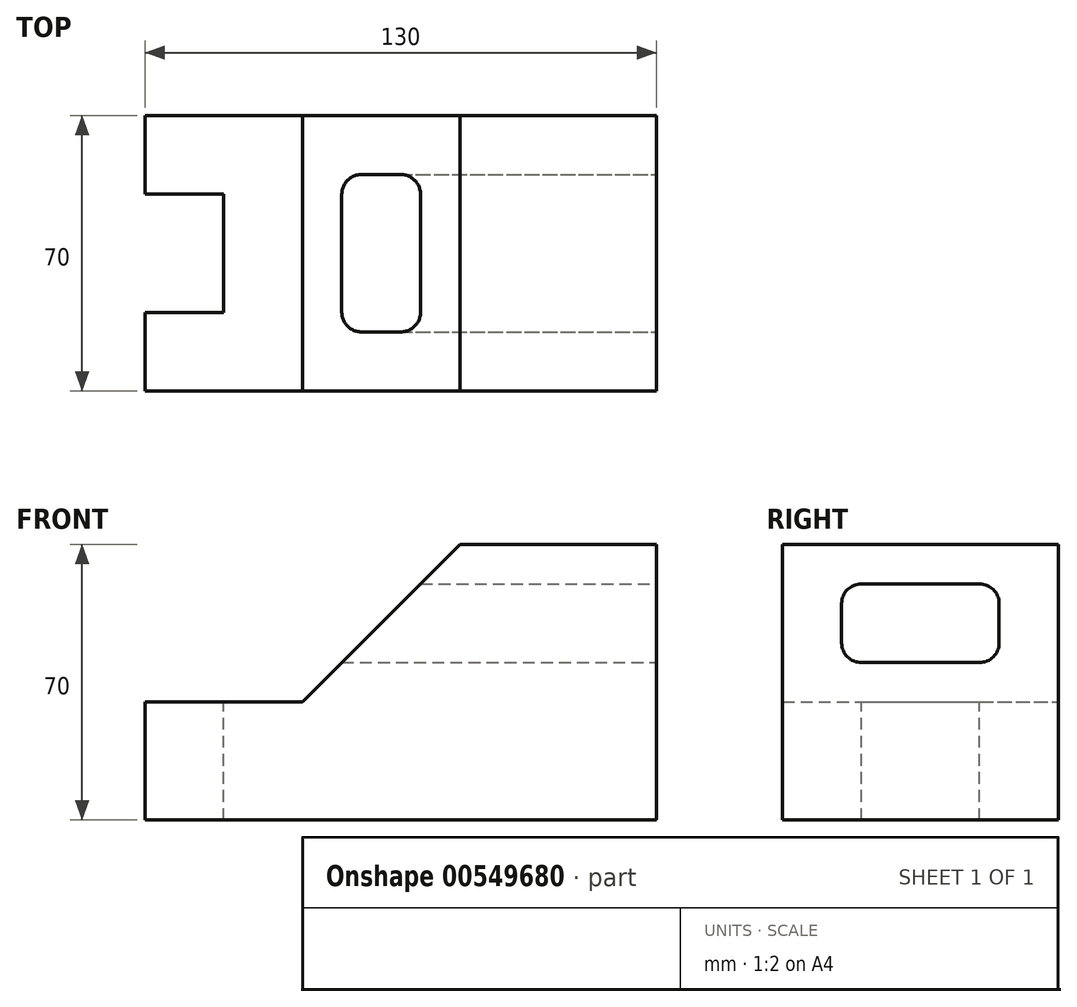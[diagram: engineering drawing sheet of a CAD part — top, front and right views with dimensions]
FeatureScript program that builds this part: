
annotation { "Feature Type Name" : "Feature", "Feature Type Description" : "" }
export const myFeature = defineFeature(function(context is Context, id is Id, definition is map)
    precondition{}
    {
        {
            var Q0;
            Q0=qCreatedBy(makeId("Front.planeOp"),FACE);
            var sketch = newSketch(context, id + "F0", { "sketchPlane" : qUnion([Q0])});
            skLineSegment(sketch, "E0.bottom", {"start": v(15, 35) * mm, "end": v(65, 35) * mm});
            skLineSegment(sketch, "E0.top", {"start": v(-65, -35) * mm, "end": v(65, -35) * mm});
            skLineSegment(sketch, "E0.left", {"start": v(-65, -5) * mm, "end": v(-65, -35) * mm});
            skLineSegment(sketch, "E0.right", {"start": v(65, 35) * mm, "end": v(65, -35) * mm});
            skPoint(sketch, "E0.middle", {"position": v(0, 0) * mm});
            skLineSegment(sketch, "E1", {"start": v(-65, -5) * mm, "end": v(-25, -5) * mm});
            skLineSegment(sketch, "E2", {"start": v(-25, -5) * mm, "end": v(15, 35) * mm});
            skPoint(sketch, "E3.orphan", {"position": v(-65, 35) * mm});
            skSolve(sketch);
        }
        {
            var Q0;
            Q0 = qSketchRegion(id + "F0", true);
            extrude(context, id + "F1", {"entities" : qUnion([Q0]), "depth" : 70 * mm, "offsetDistance" : 25 * mm});
        }
        {
            var Q0;
            Q0=makeQuery(id+"F1.opExtrude","SWEPT_FACE",FACE,{"disambiguationData":[OSD([sQuery(id+"F0.wireOp",EDGE,"E0.right")])]});
            var sketch = newSketch(context, id + "F2", { "sketchPlane" : qUnion([Q0])});
            skLineSegment(sketch, "E4", {"start": v(-55, 5) * mm, "end": v(-55, 25) * mm});
            skLineSegment(sketch, "E5", {"start": v(-55, 25) * mm, "end": v(-15, 25) * mm});
            skLineSegment(sketch, "E6", {"start": v(-15, 25) * mm, "end": v(-15, 5) * mm});
            skLineSegment(sketch, "E7", {"start": v(-15, 5) * mm, "end": v(-55, 5) * mm});
            skPoint(sketch, "E8", {"position": v(-35, 25) * mm});
            skPoint(sketch, "E9", {"position": v(-35, 35) * mm});
            skSolve(sketch);
        }
        {
            var Q0;
            Q0 = qSketchRegion(id + "F2", true);
            extrude(context, id + "F3", {"entities" : qUnion([Q0]), "operationType" : NewBodyOperationType.REMOVE, "endBound" : BoundingType.THROUGH_ALL, "oppositeDirection" : true, "depth" : 25 * mm, "offsetDistance" : 25 * mm});
        }
        {
            var Q0;
            Q0=makeQuery(id+"F3.boolean.opBoolean","COPY",EDGE,{"derivedFrom":makeQuery(id+"F3.opExtrude","SWEPT_EDGE",EDGE,{"disambiguationData":[OSD([sQuery(id+"F2.wireOp",EDGE,"E4"),sQuery(id+"F2.wireOp",EDGE,"E7")])]})});
            var Q1;
            Q1=makeQuery(id+"F3.boolean.opBoolean","COPY",EDGE,{"derivedFrom":makeQuery(id+"F3.opExtrude","SWEPT_EDGE",EDGE,{"disambiguationData":[OSD([sQuery(id+"F2.wireOp",EDGE,"E6"),sQuery(id+"F2.wireOp",EDGE,"E7")])]})});
            var Q2;
            Q2=makeQuery(id+"F3.boolean.opBoolean","COPY",EDGE,{"derivedFrom":makeQuery(id+"F3.opExtrude","SWEPT_EDGE",EDGE,{"disambiguationData":[OSD([sQuery(id+"F2.wireOp",EDGE,"E5"),sQuery(id+"F2.wireOp",EDGE,"E6")])]})});
            var Q3;
            Q3=makeQuery(id+"F3.boolean.opBoolean","COPY",EDGE,{"derivedFrom":makeQuery(id+"F3.opExtrude","SWEPT_EDGE",EDGE,{"disambiguationData":[OSD([sQuery(id+"F2.wireOp",EDGE,"E4"),sQuery(id+"F2.wireOp",EDGE,"E5")])]})});
            fillet(context, id + "F4", {"entities" : qUnion([Q0, Q1, Q2, Q3]), "radius" : 5 * mm, "tangentPropagation" : true, "allowEdgeOverflow" : false});
        }
        {
            var Q0;
            Q0=makeQuery(id+"F1.opExtrude","SWEPT_FACE",FACE,{"disambiguationData":[OSD([sQuery(id+"F0.wireOp",EDGE,"E0.left")])]});
            var sketch = newSketch(context, id + "F5", { "sketchPlane" : qUnion([Q0])});
            skLineSegment(sketch, "E10.bottom", {"start": v(50, -35) * mm, "end": v(20, -35) * mm});
            skLineSegment(sketch, "E10.top", {"start": v(50, -5) * mm, "end": v(20, -5) * mm});
            skLineSegment(sketch, "E10.left", {"start": v(50, -35) * mm, "end": v(50, -5) * mm});
            skLineSegment(sketch, "E10.right", {"start": v(20, -35) * mm, "end": v(20, -5) * mm});
            skPoint(sketch, "E10.middle", {"position": v(35, -20) * mm});
            skPoint(sketch, "E10.middle.positionSnap0", {"position": v(35, -35) * mm});
            skPoint(sketch, "E10.middle.positionSnap1", {"position": v(70, -20) * mm});
            skPoint(sketch, "E10.centerSnap0", {"position": v(35, -35) * mm});
            skPoint(sketch, "E10.centerSnap1", {"position": v(70, -20) * mm});
            skSolve(sketch);
        }
        {
            var Q0;
            Q0 = qSketchRegion(id + "F5", true);
            extrude(context, id + "F6", {"entities" : qUnion([Q0]), "operationType" : NewBodyOperationType.REMOVE, "oppositeDirection" : true, "depth" : 20 * mm, "offsetDistance" : 25 * mm});
        }
    });
